FCSTD DOCUMENT  (FreeCAD 0.16R6704 (Git))
Label: inround
License: All rights reserved
LicenseURL: http://en.wikipedia.org/wiki/All_rights_reserved
objects: Sketcher::SketchObject×1
note: 1 computed .brp shape members not serialized (recipe doc carries the construction recipe); baked Part::Feature solids carry a one-line shape summary decoded from their .brp

FEATURE [Sketcher::SketchObject] Sketch
  sketch-geometry (11):
    g0: LineSegment StartX=10 StartY=0 StartZ=0 EndX=8 EndY=-3.4641 EndZ=0
    g1: LineSegment StartX=8 StartY=-3.4641 StartZ=0 EndX=2 EndY=-3.4641 EndZ=0
    g2: LineSegment StartX=2 StartY=-3.4641 StartZ=0 EndX=0 EndY=0 EndZ=0
    g3: LineSegment StartX=0 StartY=0 StartZ=0 EndX=3 EndY=0 EndZ=0
    g4: LineSegment StartX=10 StartY=0 StartZ=0 EndX=7 EndY=0 EndZ=0
    g5: ArcOfEllipse CenterX=5 CenterY=-0.6 CenterZ=0 NormalX=0 NormalY=0 NormalZ=1 MajorRadius=2.5 MinorRadius=1 AngleXU=-3.14159 StartAngle=5.63968 EndAngle=10.0683
    g6: LineSegment [constr] StartX=2.5 StartY=-0.6 StartZ=0 EndX=7.5 EndY=-0.6 EndZ=0
    g7: LineSegment [constr] StartX=5 StartY=-1.6 StartZ=0 EndX=5 EndY=0.4 EndZ=0
    g8: GeomPoint [constr] X=2.70871 Y=-0.6 Z=0
    g9: GeomPoint [constr] X=7.29129 Y=-0.6 Z=0
    g10: LineSegment [constr] StartX=3 StartY=0 StartZ=0 EndX=7 EndY=0 EndZ=0
  constraints (22):
    c: PointOnObject(g0,g-1)
    c: Coincident(g0,g1)
    c: Horizontal(g1)
    c: Coincident(g1,g2)
    c: Angle(g2,g-1) = 1.0472
    c: DistanceX(g-1,g0) = 10
    c: Distance(g0) = 4
    c: Coincident(g2,g-1)
    c: Equal(g2,g0)
    c: Coincident(g3,g-1)
    c: Coincident(g4,g0)
    c: PointOnObject(g10,g-1)
    c: Equal(g3,g4)
    c: DistanceX(g3,g10) = 3
    c: InternalAlignment(g6-g9 -> g5) x4
    c: PointOnObject(g10,g5)
    c: DistanceY(g7,g7) = 2
    c: DistanceX(g6,g6) = 5
    c: Vertical(g7)
    c: PointOnObject(g10,g5)
    c: Horizontal(g3)
    c: Coincident(g5,g3)
